# Revit family: Basketball_Backstop-Outdoor-Heavy_Duty-IPIbyBison-PR52
name_source: partatom
category: Specialty Equipment
units: mm (PartAtom-declared; Revit-internal decimal feet)

## family parameters
Always vertical = Yes
Cut with Voids When Loaded = No
Maintain Annotation Orientation = No
OmniClass Number = 23.40.50.34.14
OmniClass Title = Gymnasium Equipment
Part Type = Normal
Room Calculation Point = No
Round Connector Dimension = Use Diameter
Shared = No
Work Plane-Based = No

## types (1)
- Outdoor System Heavy Duty
    Backboard Finish = Powder Coat - White
    Backboard Height = 2' - 11 1/2"
    Backboard Length = 4' - 6"
    Basket Netting = Finish - IPI by Bison - White Netting
    CAD Details = https://www.arcat.com
    Default Elevation = 0' - 0"
    Description = Outdoor Basketball Frame and Backboard Systems
    Embedding Depth = 4' - 0"
    Hoop Elevation = 10' - 0"
    Hoop Finish = Powder Coat - Playground Orange
    Keynote = 11 66 00
    Manufacturer = IPI by Bison
    Model = PR52
    Padding = Plastic - IPI by Bison - Scarlet SC
    Pole Material = Steel - Galvanized - Hot Dipped
    Post Diameter = 0' - 4 1/2"
    Product Page URL = https://www.arcat.com
    Specification = https://www.arcat.com
    URL = https://ipibybison.com

## geometry (parser evidence)
native form markers: Sweep x6
no freeform markers — native parametric forms only
